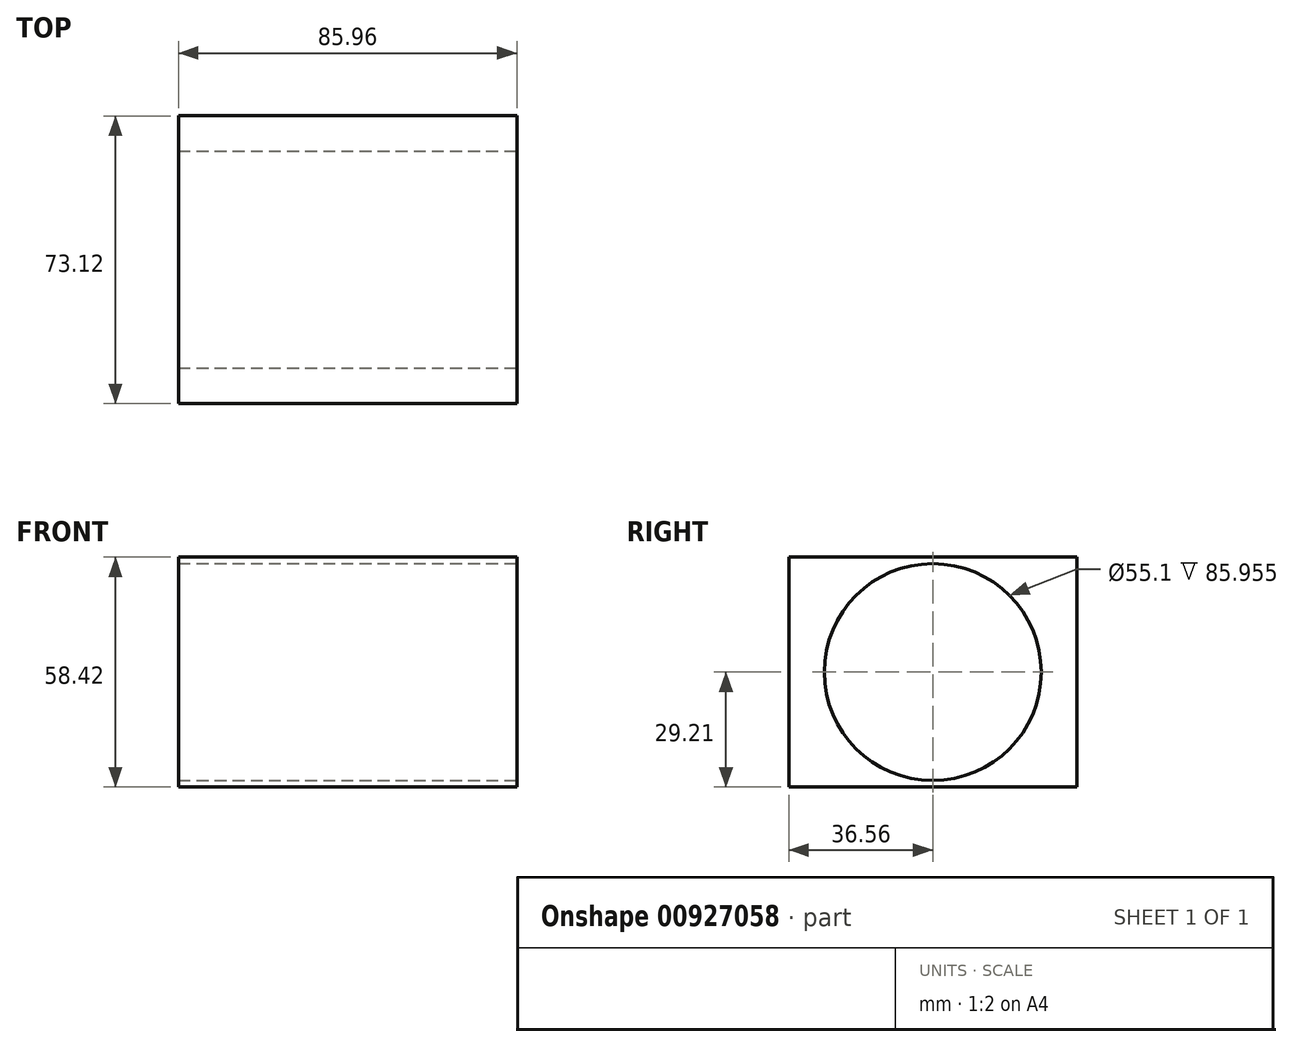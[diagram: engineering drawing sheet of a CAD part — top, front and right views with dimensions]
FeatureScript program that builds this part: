
annotation { "Feature Type Name" : "Feature", "Feature Type Description" : "" }
export const myFeature = defineFeature(function(context is Context, id is Id, definition is map)
    precondition{}
    {
        {
            var Q0;
            Q0=qCreatedBy(makeId("Top.planeOp"),FACE);
            var sketch = newSketch(context, id + "F0", { "sketchPlane" : qUnion([Q0])});
            skLineSegment(sketch, "E0.bottom", {"start": v(-42.98, 36.56) * mm, "end": v(42.98, 36.56) * mm});
            skLineSegment(sketch, "E0.top", {"start": v(-42.98, -36.56) * mm, "end": v(42.98, -36.56) * mm});
            skLineSegment(sketch, "E0.left", {"start": v(-42.98, 36.56) * mm, "end": v(-42.98, -36.56) * mm});
            skLineSegment(sketch, "E0.right", {"start": v(42.98, 36.56) * mm, "end": v(42.98, -36.56) * mm});
            skPoint(sketch, "E0.middle", {"position": v(0, 0) * mm});
            skSolve(sketch);
        }
        {
            var Q0;
            Q0=makeQuery(id+"F0.imprint","IMPRINT",FACE,{"disambiguationData":[TD([[makeQuery(id+"F0.imprint","IMPRINT",EDGE,{"derivedFrom":sQuery(id+"F0.wireOp",EDGE,"E0.bottom")}),-1.0]])]});
            extrude(context, id + "F1", {"entities" : qUnion([Q0]), "depth" : 58.42 * mm, "offsetDistance" : 25.4 * mm});
        }
        {
            var Q0;
            Q0=makeQuery(id+"F1.opExtrude","SWEPT_FACE",FACE,{"disambiguationData":[OSD([sQuery(id+"F0.wireOp",EDGE,"E0.right")])]});
            var sketch = newSketch(context, id + "F2", { "sketchPlane" : qUnion([Q0])});
            skPoint(sketch, "E1", {"position": v(0, 29.21) * mm});
            skPoint(sketch, "E1.positionSnap0", {"position": v(36.56, 29.21) * mm});
            skPoint(sketch, "E1.positionSnap1", {"position": v(0, 58.42) * mm});
            skCircle(sketch, "E2", {"center": v(0, 29.21) * mm, "radius": 27.55 * mm});
            skSolve(sketch);
        }
        {
            var Q0;
            Q0=makeQuery(id+"F2.imprint","IMPRINT",FACE,{"disambiguationData":[TD([[makeQuery(id+"F2.imprint","IMPRINT",EDGE,{"derivedFrom":sQuery(id+"F2.wireOp",EDGE,"E2")}),1.0]])]});
            extrude(context, id + "F3", {"entities" : qUnion([Q0]), "operationType" : NewBodyOperationType.REMOVE, "oppositeDirection" : true, "depth" : 86.36 * mm, "offsetDistance" : 25.4 * mm});
        }
    });
